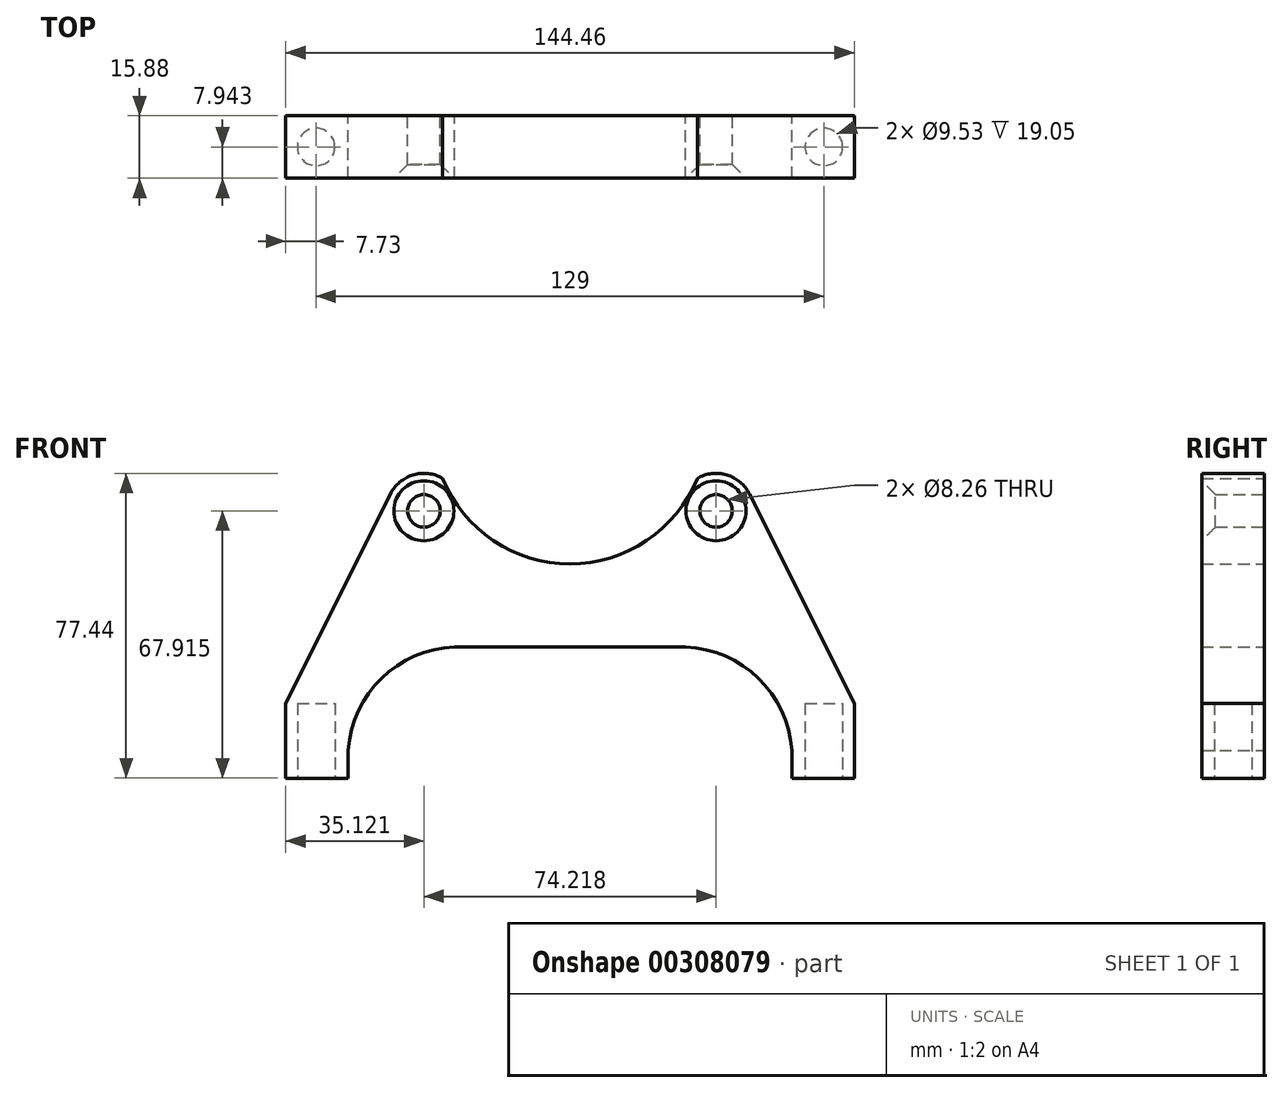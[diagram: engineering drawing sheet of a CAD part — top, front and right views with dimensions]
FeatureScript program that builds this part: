
annotation { "Feature Type Name" : "Feature", "Feature Type Description" : "" }
export const myFeature = defineFeature(function(context is Context, id is Id, definition is map)
    precondition{}
    {
        {
            var Q0;
            Q0=qCreatedBy(makeId("Front.planeOp"),FACE);
            var sketch = newSketch(context, id + "F0", { "sketchPlane" : qUnion([Q0])});
            skArc(sketch, "E0", {"start": v(-32.34, -13.18) * mm, "mid": v(0, -34.92) * mm, "end": v(32.34, -13.18) * mm});
            skCircle(sketch, "E1", {"center": v(-37.1, -21.42) * mm, "radius": 4.13 * mm});
            skArc(sketch, "E2", {"start": v(-32.34, -13.18) * mm, "mid": v(-39.84, -12.3) * mm, "end": v(-45.63, -17.16) * mm});
            skCircle(sketch, "E3.MirrorC", {"center": v(37.1, -21.42) * mm, "radius": 4.13 * mm});
            skArc(sketch, "E4.MirrorCS", {"start": v(32.34, -13.18) * mm, "mid": v(39.84, -12.3) * mm, "end": v(45.63, -17.16) * mm});
            skPoint(sketch, "E5.orphan", {"position": v(0, -34.93) * mm});
            skLineSegment(sketch, "E6.0", {"start": v(-29.37, -56) * mm, "end": v(29.37, -56) * mm});
            skLineSegment(sketch, "E7.0", {"start": v(-72.23, -89.34) * mm, "end": v(-56.36, -89.34) * mm});
            skLineSegment(sketch, "E8", {"start": v(0, -34.93) * mm, "end": v(0, -56) * mm});
            skLineSegment(sketch, "E9.0", {"start": v(72.23, -70.3) * mm, "end": v(72.23, -89.34) * mm});
            skLineSegment(sketch, "E10.0", {"start": v(-72.23, -70.3) * mm, "end": v(-72.23, -89.34) * mm});
            skLineSegment(sketch, "E11.0", {"start": v(56.36, -82.25) * mm, "end": v(56.36, -89.34) * mm});
            skLineSegment(sketch, "E12.0", {"start": v(-56.36, -82.25) * mm, "end": v(-56.36, -89.34) * mm});
            skArc(sketch, "E13", {"start": v(56.36, -86.17) * mm, "mid": v(48.44, -64.53) * mm, "end": v(27.03, -56) * mm});
            skPoint(sketch, "E13.first.point", {"position": v(56.36, -86.17) * mm});
            skPoint(sketch, "E13.second.point", {"position": v(27.03, -56) * mm});
            skLineSegment(sketch, "E14.trimOffspring", {"start": v(55.95, -89.34) * mm, "end": v(72.23, -89.34) * mm});
            skArc(sketch, "E15.MirrorCS", {"start": v(-56.36, -86.17) * mm, "mid": v(-48.44, -64.53) * mm, "end": v(-27.03, -56) * mm});
            skPoint(sketch, "E16.endSnap0", {"position": v(45.36, -26.19) * mm});
            skLineSegment(sketch, "E17", {"start": v(-72.23, -70.3) * mm, "end": v(-45.63, -17.16) * mm});
            skLineSegment(sketch, "E18", {"start": v(72.23, -70.3) * mm, "end": v(45.63, -17.16) * mm});
            skPoint(sketch, "E19.orphan", {"position": v(27.58, -21.42) * mm});
            skPoint(sketch, "E20.orphan", {"position": v(-27.58, -21.42) * mm});
            skSolve(sketch);
        }
        {
            var Q0;
            Q0 = qSketchRegion(id + "F0", true);
            extrude(context, id + "F1", {"entities" : qUnion([Q0]), "depth" : 15.88 * mm, "offsetDistance" : 25.4 * mm});
        }
        {
            var Q0;
            Q0=makeQuery(id+"F1.opExtrude","CAP_FACE",FACE,{"disambiguationData":[OSD([sQuery(id+"F0.wireOp",EDGE,"E0"),sQuery(id+"F0.wireOp",EDGE,"E1"),sQuery(id+"F0.wireOp",EDGE,"E2"),sQuery(id+"F0.wireOp",EDGE,"E3.MirrorC"),sQuery(id+"F0.wireOp",EDGE,"E4.MirrorCS"),sQuery(id+"F0.wireOp",EDGE,"E6.0"),sQuery(id+"F0.wireOp",EDGE,"E7.0"),sQuery(id+"F0.wireOp",EDGE,"E9.0"),sQuery(id+"F0.wireOp",EDGE,"E10.0"),sQuery(id+"F0.wireOp",EDGE,"E11.0"),sQuery(id+"F0.wireOp",EDGE,"E12.0"),sQuery(id+"F0.wireOp",EDGE,"E13"),sQuery(id+"F0.wireOp",EDGE,"E14.trimOffspring"),sQuery(id+"F0.wireOp",EDGE,"E15.MirrorCS"),sQuery(id+"F0.wireOp",EDGE,"E17"),sQuery(id+"F0.wireOp",EDGE,"E18")])],"isStart":false});
            var sketch = newSketch(context, id + "F2", { "sketchPlane" : qUnion([Q0])});
            skArc(sketch, "E21.0", {"start": v(-32.34, -13.18) * mm, "mid": v(0, -34.92) * mm, "end": v(32.34, -13.18) * mm});
            skCircle(sketch, "E21.1", {"center": v(-37.1, -21.42) * mm, "radius": 4.13 * mm});
            skArc(sketch, "E21.2", {"start": v(-32.34, -13.18) * mm, "mid": v(-39.84, -12.3) * mm, "end": v(-45.63, -17.16) * mm});
            skCircle(sketch, "E21.3", {"center": v(37.1, -21.42) * mm, "radius": 4.13 * mm});
            skArc(sketch, "E21.4", {"start": v(32.34, -13.18) * mm, "mid": v(39.84, -12.3) * mm, "end": v(45.63, -17.16) * mm});
            skPoint(sketch, "E21.5", {"position": v(0, -34.93) * mm});
            skLineSegment(sketch, "E21.6", {"start": v(-29.37, -56) * mm, "end": v(29.37, -56) * mm});
            skLineSegment(sketch, "E21.7", {"start": v(-72.23, -89.34) * mm, "end": v(-56.36, -89.34) * mm});
            skLineSegment(sketch, "E21.8", {"start": v(0, -34.93) * mm, "end": v(0, -56) * mm});
            skLineSegment(sketch, "E21.9", {"start": v(72.23, -70.3) * mm, "end": v(72.23, -89.34) * mm});
            skLineSegment(sketch, "E21.10", {"start": v(-72.23, -70.3) * mm, "end": v(-72.23, -89.34) * mm});
            skLineSegment(sketch, "E21.11", {"start": v(56.36, -82.25) * mm, "end": v(56.36, -89.34) * mm});
            skLineSegment(sketch, "E21.12", {"start": v(-56.36, -82.25) * mm, "end": v(-56.36, -89.34) * mm});
            skArc(sketch, "E21.13", {"start": v(56.36, -86.17) * mm, "mid": v(48.44, -64.53) * mm, "end": v(27.03, -56) * mm});
            skPoint(sketch, "E21.14", {"position": v(56.36, -86.17) * mm});
            skPoint(sketch, "E21.15", {"position": v(27.03, -56) * mm});
            skLineSegment(sketch, "E21.17", {"start": v(55.95, -89.34) * mm, "end": v(72.23, -89.34) * mm});
            skArc(sketch, "E21.18", {"start": v(-56.36, -86.17) * mm, "mid": v(-48.44, -64.53) * mm, "end": v(-27.03, -56) * mm});
            skPoint(sketch, "E21.22", {"position": v(45.36, -26.19) * mm});
            skLineSegment(sketch, "E21.23", {"start": v(-72.23, -70.3) * mm, "end": v(-45.63, -17.16) * mm});
            skLineSegment(sketch, "E21.24", {"start": v(72.23, -70.3) * mm, "end": v(45.63, -17.16) * mm});
            skPoint(sketch, "E21.25", {"position": v(27.58, -21.42) * mm});
            skPoint(sketch, "E21.26", {"position": v(-27.58, -21.42) * mm});
            skSolve(sketch);
        }
        {
            var Q0;
            Q0=sQuery(id+"F2.wireOp",VERTEX,"E21.1.center");
            var Q1;
            Q1=sQuery(id+"F2.wireOp",VERTEX,"E21.3.center");
            var Q2;
            Q2=makeQuery(id+"F1.opExtrude","SWEPT_BODY",BODY,{"disambiguationData":[OSD([sQuery(id+"F0.wireOp",EDGE,"E0"),sQuery(id+"F0.wireOp",EDGE,"E1"),sQuery(id+"F0.wireOp",EDGE,"E2"),sQuery(id+"F0.wireOp",EDGE,"E3.MirrorC"),sQuery(id+"F0.wireOp",EDGE,"E4.MirrorCS"),sQuery(id+"F0.wireOp",EDGE,"E6.0"),sQuery(id+"F0.wireOp",EDGE,"E7.0"),sQuery(id+"F0.wireOp",EDGE,"E9.0"),sQuery(id+"F0.wireOp",EDGE,"E10.0"),sQuery(id+"F0.wireOp",EDGE,"E11.0"),sQuery(id+"F0.wireOp",EDGE,"E12.0"),sQuery(id+"F0.wireOp",EDGE,"E13"),sQuery(id+"F0.wireOp",EDGE,"E14.trimOffspring"),sQuery(id+"F0.wireOp",EDGE,"E15.MirrorCS"),sQuery(id+"F0.wireOp",EDGE,"E17"),sQuery(id+"F0.wireOp",EDGE,"E18")])]});
            hole(context, id + "F3", {"style" : HoleStyle.C_SINK, "endStyle" : HoleEndStyle.BLIND, "holeDiameter" : 8.25 * mm, "cSinkDiameter" : 15.24 * mm, "cSinkAngle" : 90 * degree, "majorDiameter" : 6.35 * mm, "holeDepth" : 25.4 * mm, "isTappedThrough" : true, "tappedDepth" : 12.7 * mm, "tapClearance" : 3, "locations" : qUnion([Q0, Q1]), "scope" : qUnion([Q2])});
        }
        {
            var Q0;
            Q0=makeQuery(id+"F1.opExtrude","SWEPT_FACE",FACE,{"disambiguationData":[OSD([sQuery(id+"F0.wireOp",EDGE,"E7.0")])]});
            var sketch = newSketch(context, id + "F4", { "sketchPlane" : qUnion([Q0])});
            skLineSegment(sketch, "E22.0", {"start": v(-72.23, 15.88) * mm, "end": v(-56.36, 15.88) * mm});
            skLineSegment(sketch, "E22.1", {"start": v(-72.23, 15.88) * mm, "end": v(-72.23, 0) * mm});
            skLineSegment(sketch, "E22.2", {"start": v(-72.23, 0) * mm, "end": v(-56.36, 0) * mm});
            skLineSegment(sketch, "E22.3", {"start": v(56.36, 15.88) * mm, "end": v(72.23, 15.88) * mm});
            skLineSegment(sketch, "E22.4", {"start": v(72.23, 15.88) * mm, "end": v(72.23, 0) * mm});
            skLineSegment(sketch, "E22.5", {"start": v(56.36, 0) * mm, "end": v(72.23, 0) * mm});
            skPoint(sketch, "E22.6", {"position": v(-72.23, 7.94) * mm});
            skLineSegment(sketch, "E23", {"start": v(-72.23, 7.94) * mm, "end": v(72.23, 7.94) * mm, "construction": true});
            skLineSegment(sketch, "E24", {"start": v(0, 7.94) * mm, "end": v(0, 38.13) * mm, "construction": true});
            skLineSegment(sketch, "E25.0", {"start": v(-64.5, 7.94) * mm, "end": v(-64.5, 38.13) * mm, "construction": true});
            skLineSegment(sketch, "E26", {"start": v(64.5, 7.94) * mm, "end": v(64.5, 36.59) * mm, "construction": true});
            skCircle(sketch, "E27", {"center": v(-64.5, 7.94) * mm, "radius": 4.76 * mm});
            skCircle(sketch, "E28", {"center": v(64.5, 7.94) * mm, "radius": 4.76 * mm});
            skSolve(sketch);
        }
        {
            var Q0;
            Q0 = qSketchRegion(id + "F4", true);
            extrude(context, id + "F5", {"entities" : qUnion([Q0]), "operationType" : NewBodyOperationType.REMOVE, "oppositeDirection" : true, "depth" : 19.05 * mm, "offsetDistance" : 25.4 * mm});
        }
    });
